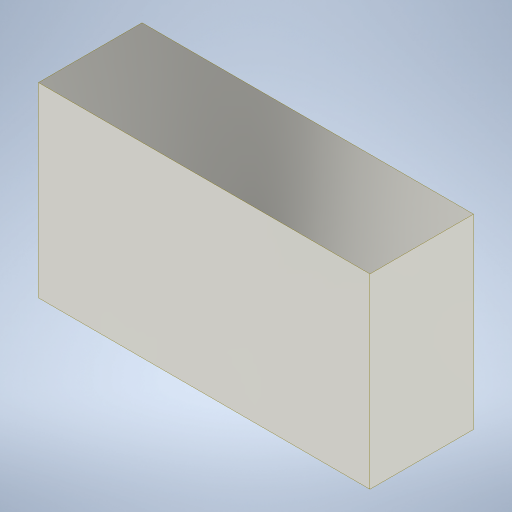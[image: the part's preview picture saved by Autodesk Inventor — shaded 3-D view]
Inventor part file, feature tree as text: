
AUTODESK INVENTOR PART (.ipt)
format: ipt  version: 2023 (Build 270158000, 158)  size: 174,080 bytes
history: native  units: mm
features: extrude x1, sketch x1
ambient origin geometry x8: Origin, YZ Plane, XZ Plane, XY Plane, X Axis, Y Axis, Z Axis, Center Point
bodies: Volumenkörper1 (feature_tree)
feature tree (2):
  extrude  "Extrusion1"  Depth=1.6mm
  sketch  "Skizze1"  dims[d0=0.9mm d1=1.6mm d2=0.5mm d3=0.0mm]
